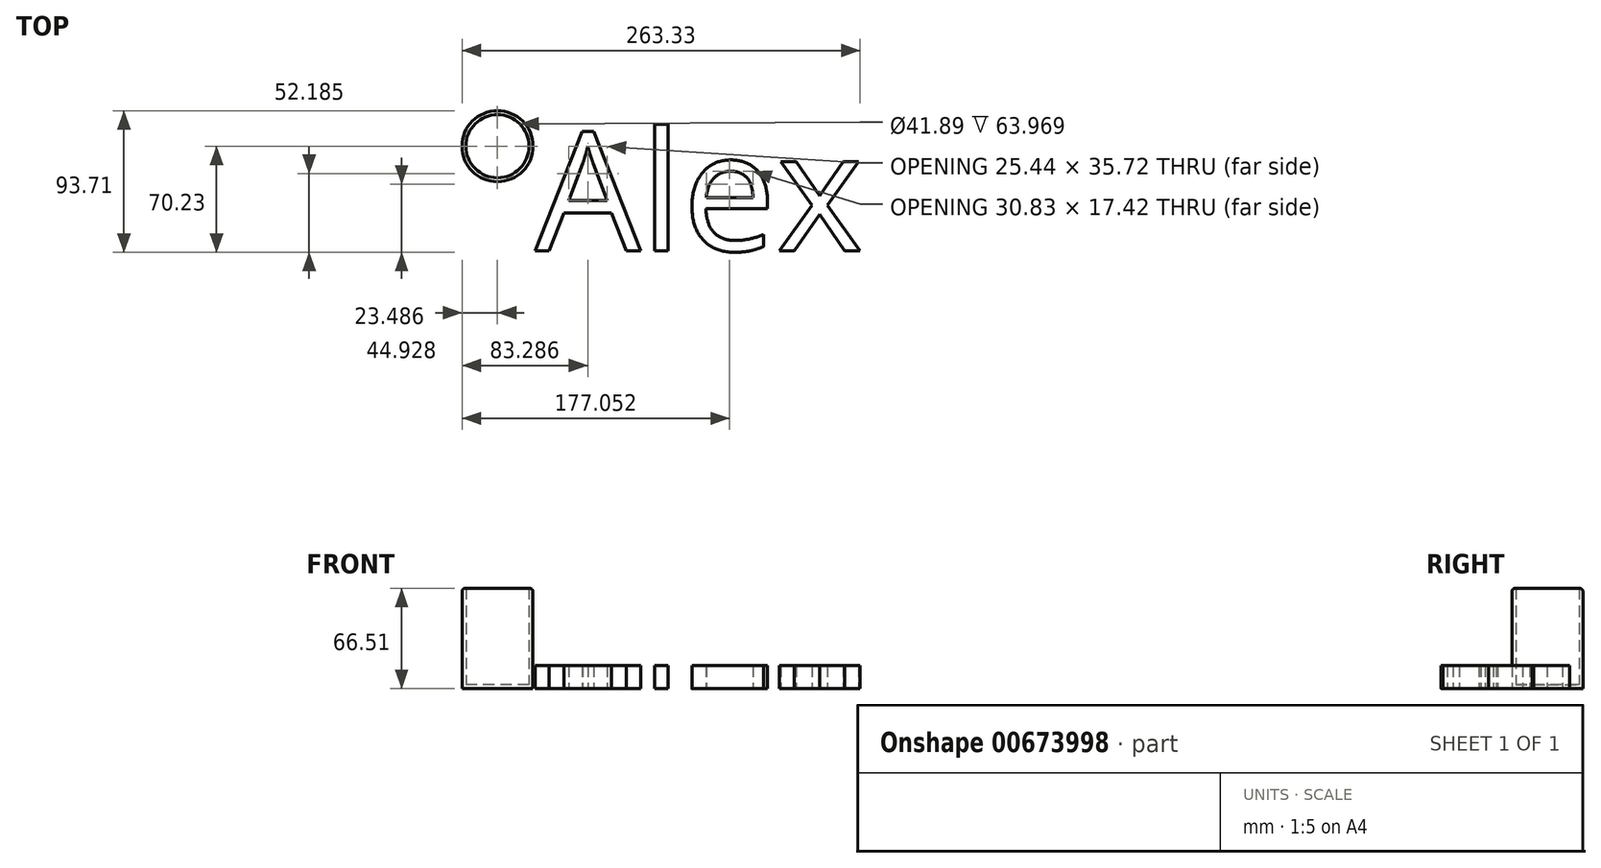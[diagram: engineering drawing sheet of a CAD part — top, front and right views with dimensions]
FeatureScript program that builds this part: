
annotation { "Feature Type Name" : "Feature", "Feature Type Description" : "" }
export const myFeature = defineFeature(function(context is Context, id is Id, definition is map)
    precondition{}
    {
        {
            var Q0;
            Q0=qCreatedBy(makeId("Top.planeOp"),FACE);
            var sketch = newSketch(context, id + "F0", { "sketchPlane" : qUnion([Q0])});
            skCircle(sketch, "E0", {"center": v(-7.28, 27.61) * mm, "radius": 23.48 * mm});
            skSolve(sketch);
        }
        {
            var Q0;
            Q0=makeQuery(id+"F0.imprint","IMPRINT",FACE,{"disambiguationData":[TD([[makeQuery(id+"F0.imprint","IMPRINT",EDGE,{"derivedFrom":sQuery(id+"F0.wireOp",EDGE,"E0")}),1.0]])]});
            extrude(context, id + "F1", {"entities" : qUnion([Q0]), "depth" : 66.5 * mm, "offsetDistance" : 25.4 * mm});
        }
        {
            var Q0;
            Q0=makeQuery(id+"F1.opExtrude","CAP_FACE",FACE,{"disambiguationData":[OSD([sQuery(id+"F0.wireOp",EDGE,"E0")])],"isStart":false});
            shell(context, id + "F2", {"entities" : qUnion([Q0]), "thickness" : 2.54 * mm});
        }
        {
            var Q0;
            Q0=makeQuery(id+"F1.opExtrude","CAP_EDGE",EDGE,{"disambiguationData":[OSD([sQuery(id+"F0.wireOp",EDGE,"E0")])],"isStart":false});
            fillet(context, id + "F3", {"entities" : qUnion([Q0]), "radius" : 2.35 * mm, "tangentPropagation" : true, "allowEdgeOverflow" : false});
        }
        {
            var Q0;
            Q0=qCreatedBy(makeId("Top.planeOp"),FACE);
            var sketch = newSketch(context, id + "F4", { "sketchPlane" : qUnion([Q0])});
            skText(sketch, "E1", { "text": "Alex", "fontName": "OpenSans-Regular.ttf"});
            const initialGuessF4  = {"E1": [0.01762, -0.04154, 1, 0, 0.07933]};
            skSetInitialGuess(sketch, initialGuessF4);
            skSolve(sketch);
        }
        {
            var Q0;
            Q0 = qSketchRegion(id + "F4", true);
            extrude(context, id + "F5", {"entities" : qUnion([Q0]), "depth" : 15.34 * mm, "offsetDistance" : 25.4 * mm});
        }
    });
